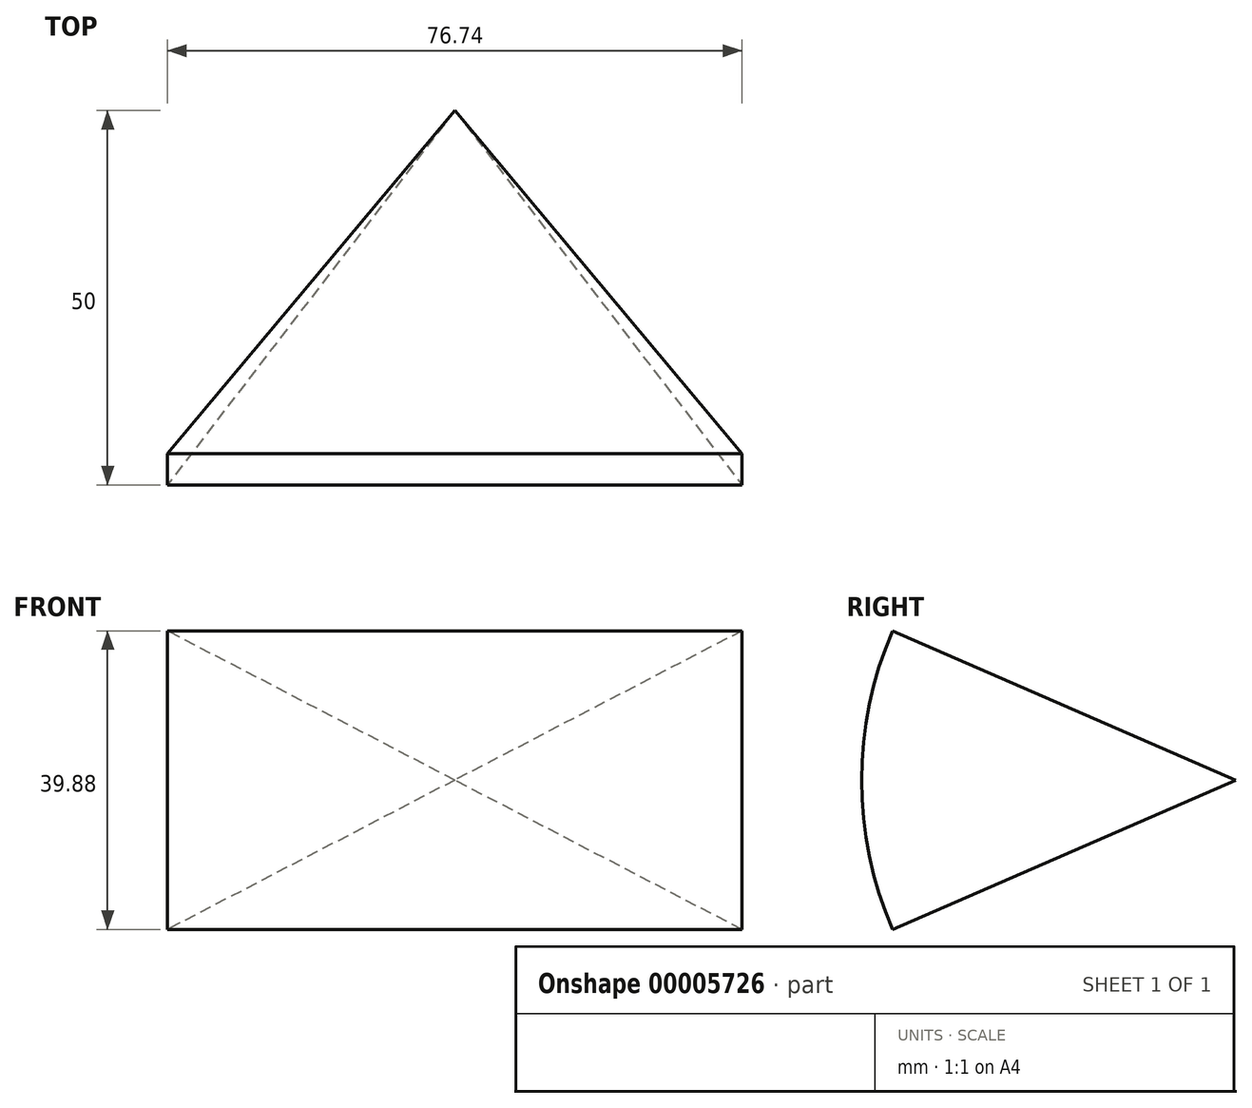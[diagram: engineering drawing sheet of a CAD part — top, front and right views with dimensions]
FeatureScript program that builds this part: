
annotation { "Feature Type Name" : "Feature", "Feature Type Description" : "" }
export const myFeature = defineFeature(function(context is Context, id is Id, definition is map)
    precondition{}
    {
        {
            var Q0;
            Q0=qCreatedBy(makeId("Top.planeOp"),FACE);
            var sketch = newSketch(context, id + "F0", { "sketchPlane" : qUnion([Q0])});
            skLineSegment(sketch, "E0", {"start": v(0, 0) * mm, "end": v(-38.37, -50) * mm});
            skLineSegment(sketch, "E1", {"start": v(-38.37, -50) * mm, "end": v(38.37, -50) * mm});
            skLineSegment(sketch, "E2", {"start": v(38.37, -50) * mm, "end": v(0, 0) * mm});
            skLineSegment(sketch, "E3", {"start": v(0, 0) * mm, "end": v(0, 27.44) * mm});
            skLineSegment(sketch, "E4", {"start": v(-22.46, 0) * mm, "end": v(23.86, 0) * mm});
            skSolve(sketch);
        }
        {
            var Q0;
            Q0=makeQuery(id+"F0.imprint","IMPRINT",FACE,{"disambiguationData":[TD([[makeQuery(id+"F0.imprint","IMPRINT",EDGE,{"derivedFrom":sQuery(id+"F0.wireOp",EDGE,"E0")}),1.0]])]});
            var Q1;
            Q1=sQuery(id+"F0.wireOp",EDGE,"E4");
            revolve(context, id + "F1", {"entities" : qUnion([Q0]), "axis" : qUnion([Q1]), "revolveType" : RevolveType.SYMMETRIC, "angle" : 47 * degree});
        }
    });
